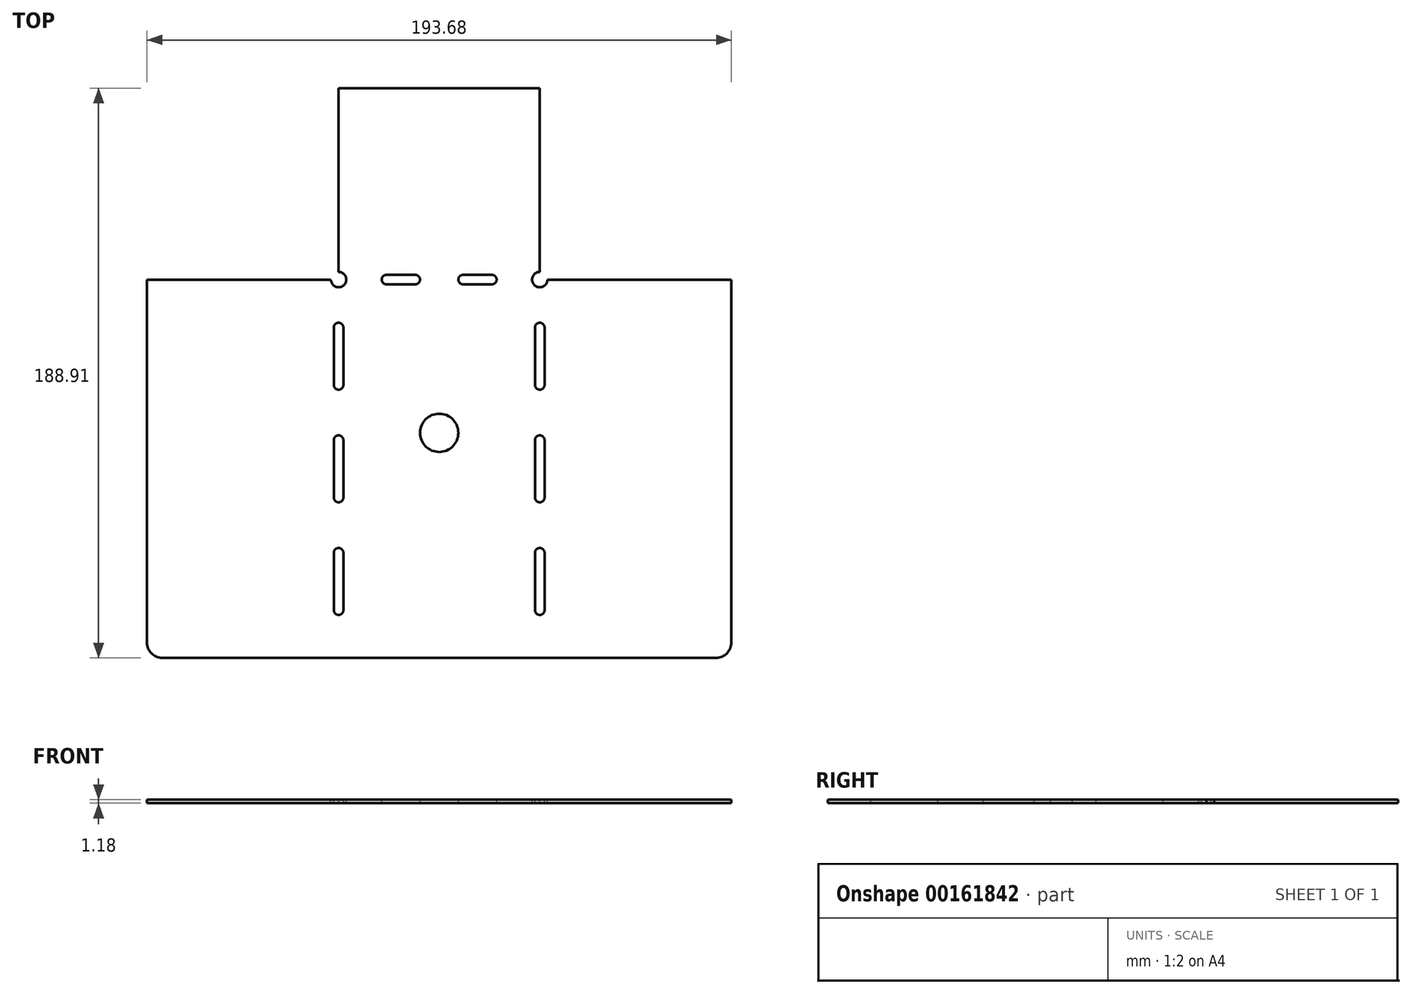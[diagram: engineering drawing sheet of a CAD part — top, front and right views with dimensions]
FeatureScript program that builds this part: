
annotation { "Feature Type Name" : "Feature", "Feature Type Description" : "" }
export const myFeature = defineFeature(function(context is Context, id is Id, definition is map)
    precondition{}
    {
        {
            var Q0;
            Q0=qCreatedBy(makeId("Top.planeOp"),FACE);
            var sketch = newSketch(context, id + "F0", { "sketchPlane" : qUnion([Q0])});
            skLineSegment(sketch, "E0", {"start": v(-33.34, 0) * mm, "end": v(33.34, 0) * mm});
            skLineSegment(sketch, "E1", {"start": v(33.34, 0) * mm, "end": v(33.34, 125.41) * mm});
            skLineSegment(sketch, "E2", {"start": v(33.34, 125.41) * mm, "end": v(-33.34, 125.41) * mm});
            skLineSegment(sketch, "E3", {"start": v(-33.34, 125.41) * mm, "end": v(-33.34, 0) * mm});
            skLineSegment(sketch, "E4", {"start": v(-33.34, 125.41) * mm, "end": v(-96.84, 125.41) * mm});
            skLineSegment(sketch, "E5", {"start": v(-96.84, 125.41) * mm, "end": v(-96.84, 0) * mm});
            skLineSegment(sketch, "E6", {"start": v(-96.84, 0) * mm, "end": v(-33.34, 0) * mm});
            skLineSegment(sketch, "E7", {"start": v(33.34, 125.41) * mm, "end": v(96.84, 125.41) * mm});
            skLineSegment(sketch, "E8", {"start": v(96.84, 125.41) * mm, "end": v(96.84, 0) * mm});
            skLineSegment(sketch, "E9", {"start": v(96.84, 0) * mm, "end": v(33.34, 0) * mm});
            skLineSegment(sketch, "E10", {"start": v(33.34, 125.41) * mm, "end": v(33.34, 188.91) * mm});
            skLineSegment(sketch, "E11", {"start": v(33.34, 188.91) * mm, "end": v(-33.34, 188.91) * mm});
            skLineSegment(sketch, "E12", {"start": v(-33.34, 188.91) * mm, "end": v(-33.34, 125.41) * mm});
            skSolve(sketch);
        }
        {
            var Q0;
            Q0 = qSketchRegion(id + "F0", true);
            extrude(context, id + "F1", {"entities" : qUnion([Q0]), "depth" : 1.18 * mm});
        }
        {
            var Q0;
            Q0=makeQuery(id+"F1.opExtrude","CAP_FACE",FACE,{"disambiguationData":[OSD([sQuery(id+"F0.wireOp",EDGE,"E0"),sQuery(id+"F0.wireOp",EDGE,"E4"),sQuery(id+"F0.wireOp",EDGE,"E5"),sQuery(id+"F0.wireOp",EDGE,"E6"),sQuery(id+"F0.wireOp",EDGE,"E7"),sQuery(id+"F0.wireOp",EDGE,"E8"),sQuery(id+"F0.wireOp",EDGE,"E9"),sQuery(id+"F0.wireOp",EDGE,"E10"),sQuery(id+"F0.wireOp",EDGE,"E11"),sQuery(id+"F0.wireOp",EDGE,"E12")])],"isStart":false});
            var sketch = newSketch(context, id + "F2", { "sketchPlane" : qUnion([Q0])});
            skLineSegment(sketch, "E13", {"start": v(-33.34, 109.54) * mm, "end": v(-33.34, 90.49) * mm});
            skLineSegment(sketch, "E14", {"start": v(0, 211.66) * mm, "end": v(0, -16) * mm, "construction": true});
            skLineSegment(sketch, "E15", {"start": v(-17.46, 125.41) * mm, "end": v(-7.94, 125.41) * mm});
            skPoint(sketch, "E16", {"position": v(-33.34, 109.54) * mm});
            skPoint(sketch, "E17", {"position": v(-33.34, 90.49) * mm});
            skPoint(sketch, "E18.orphan", {"position": v(-33.34, 0) * mm});
            skLineSegment(sketch, "E19.0.1.0", {"start": v(-33.34, 72.2) * mm, "end": v(-33.34, 53.15) * mm});
            skLineSegment(sketch, "E19.0.2.0", {"start": v(-33.34, 34.86) * mm, "end": v(-33.34, 15.81) * mm});
            skLineSegment(sketch, "E19.direction1", {"start": v(-33.34, 90.49) * mm, "end": v(-7.94, 90.49) * mm, "construction": true});
            skLineSegment(sketch, "E19.direction2", {"start": v(-33.34, 72.2) * mm, "end": v(-33.34, 53.15) * mm, "construction": true});
            skLineSegment(sketch, "E20.MirrorCS", {"start": v(33.34, 109.54) * mm, "end": v(33.34, 90.49) * mm});
            skLineSegment(sketch, "E21.MirrorCS", {"start": v(33.34, 72.2) * mm, "end": v(33.34, 53.15) * mm, "construction": true});
            skLineSegment(sketch, "E22.MirrorCS", {"start": v(33.34, 34.86) * mm, "end": v(33.34, 15.81) * mm});
            skArc(sketch, "E23.0.startCap", {"start": v(-34.93, 109.54) * mm, "mid": v(-33.34, 111.13) * mm, "end": v(-31.75, 109.54) * mm});
            skArc(sketch, "E23.0.endCap", {"start": v(-31.75, 90.49) * mm, "mid": v(-33.34, 88.9) * mm, "end": v(-34.93, 90.49) * mm});
            skLineSegment(sketch, "E23.0.left", {"start": v(-31.75, 109.54) * mm, "end": v(-31.75, 90.49) * mm});
            skLineSegment(sketch, "E23.0.right", {"start": v(-34.93, 109.54) * mm, "end": v(-34.93, 90.49) * mm});
            skArc(sketch, "E23.1.startCap", {"start": v(-34.93, 72.2) * mm, "mid": v(-33.34, 73.79) * mm, "end": v(-31.75, 72.2) * mm});
            skArc(sketch, "E23.1.endCap", {"start": v(-31.75, 53.15) * mm, "mid": v(-33.34, 51.56) * mm, "end": v(-34.93, 53.15) * mm});
            skLineSegment(sketch, "E23.1.left", {"start": v(-31.75, 72.2) * mm, "end": v(-31.75, 53.15) * mm});
            skLineSegment(sketch, "E23.1.right", {"start": v(-34.92, 72.2) * mm, "end": v(-34.92, 53.15) * mm});
            skArc(sketch, "E23.2.startCap", {"start": v(-34.93, 34.86) * mm, "mid": v(-33.34, 36.45) * mm, "end": v(-31.75, 34.86) * mm});
            skArc(sketch, "E23.2.endCap", {"start": v(-31.75, 15.81) * mm, "mid": v(-33.34, 14.22) * mm, "end": v(-34.93, 15.81) * mm});
            skLineSegment(sketch, "E23.2.left", {"start": v(-31.75, 34.86) * mm, "end": v(-31.75, 15.81) * mm});
            skLineSegment(sketch, "E23.2.right", {"start": v(-34.92, 34.86) * mm, "end": v(-34.92, 15.81) * mm});
            skArc(sketch, "E23.3.startCap", {"start": v(31.75, 34.86) * mm, "mid": v(33.34, 36.45) * mm, "end": v(34.93, 34.86) * mm});
            skArc(sketch, "E23.3.endCap", {"start": v(34.93, 15.81) * mm, "mid": v(33.34, 14.22) * mm, "end": v(31.75, 15.81) * mm});
            skLineSegment(sketch, "E23.3.left", {"start": v(34.93, 34.86) * mm, "end": v(34.93, 15.81) * mm});
            skLineSegment(sketch, "E23.3.right", {"start": v(31.75, 34.86) * mm, "end": v(31.75, 15.81) * mm});
            skArc(sketch, "E23.4.startCap", {"start": v(31.75, 72.2) * mm, "mid": v(33.34, 73.79) * mm, "end": v(34.93, 72.2) * mm});
            skArc(sketch, "E23.4.endCap", {"start": v(34.93, 53.15) * mm, "mid": v(33.34, 51.56) * mm, "end": v(31.75, 53.15) * mm});
            skLineSegment(sketch, "E23.4.left", {"start": v(34.93, 72.2) * mm, "end": v(34.93, 53.15) * mm});
            skLineSegment(sketch, "E23.4.right", {"start": v(31.75, 72.2) * mm, "end": v(31.75, 53.15) * mm});
            skArc(sketch, "E23.5.startCap", {"start": v(31.75, 109.54) * mm, "mid": v(33.34, 111.13) * mm, "end": v(34.93, 109.54) * mm});
            skArc(sketch, "E23.5.endCap", {"start": v(34.93, 90.49) * mm, "mid": v(33.34, 88.9) * mm, "end": v(31.75, 90.49) * mm});
            skLineSegment(sketch, "E23.5.left", {"start": v(34.93, 109.54) * mm, "end": v(34.93, 90.49) * mm});
            skLineSegment(sketch, "E23.5.right", {"start": v(31.75, 109.54) * mm, "end": v(31.75, 90.49) * mm});
            skPoint(sketch, "E24", {"position": v(-17.46, 125.41) * mm});
            skPoint(sketch, "E25", {"position": v(-7.94, 125.41) * mm});
            skPoint(sketch, "E26", {"position": v(7.94, 125.41) * mm});
            skPoint(sketch, "E27", {"position": v(17.46, 125.41) * mm});
            skPoint(sketch, "E28.orphan", {"position": v(-33.34, 125.41) * mm});
            skPoint(sketch, "E29.orphan", {"position": v(33.34, 125.41) * mm});
            skLineSegment(sketch, "E30.trimOffspring", {"start": v(7.94, 125.41) * mm, "end": v(17.46, 125.41) * mm});
            skArc(sketch, "E31.0.startCap", {"start": v(-17.46, 123.83) * mm, "mid": v(-19.05, 125.41) * mm, "end": v(-17.46, 127) * mm});
            skArc(sketch, "E31.0.endCap", {"start": v(-7.94, 127) * mm, "mid": v(-6.35, 125.41) * mm, "end": v(-7.94, 123.83) * mm});
            skLineSegment(sketch, "E31.0.left", {"start": v(-17.46, 127) * mm, "end": v(-7.94, 127) * mm});
            skLineSegment(sketch, "E31.0.right", {"start": v(-17.46, 123.83) * mm, "end": v(-7.94, 123.83) * mm});
            skArc(sketch, "E31.1.startCap", {"start": v(7.94, 123.83) * mm, "mid": v(6.35, 125.41) * mm, "end": v(7.94, 127) * mm});
            skArc(sketch, "E31.1.endCap", {"start": v(17.46, 127) * mm, "mid": v(19.05, 125.41) * mm, "end": v(17.46, 123.83) * mm});
            skLineSegment(sketch, "E31.1.left", {"start": v(7.94, 127) * mm, "end": v(17.46, 127) * mm});
            skLineSegment(sketch, "E31.1.right", {"start": v(7.94, 123.83) * mm, "end": v(17.46, 123.83) * mm});
            skCircle(sketch, "E32", {"center": v(-33.34, 125.41) * mm, "radius": 2.54 * mm});
            skCircle(sketch, "E33", {"center": v(33.34, 125.41) * mm, "radius": 2.54 * mm});
            skCircle(sketch, "E34", {"center": v(0, 74.61) * mm, "radius": 6.35 * mm});
            skSolve(sketch);
        }
        {
            var Q0;
            Q0 = qSketchRegion(id + "F2", true);
            extrude(context, id + "F3", {"entities" : qUnion([Q0]), "operationType" : NewBodyOperationType.REMOVE, "endBound" : BoundingType.UP_TO_NEXT, "oppositeDirection" : true, "depth" : 25.4 * mm});
        }
        {
            var Q0;
            Q0=makeQuery(id+"F1.opExtrude","SWEPT_EDGE",EDGE,{"disambiguationData":[OSD([sQuery(id+"F0.wireOp",EDGE,"E5"),sQuery(id+"F0.wireOp",EDGE,"E6")])]});
            var Q1;
            Q1=makeQuery(id+"F1.opExtrude","SWEPT_EDGE",EDGE,{"disambiguationData":[OSD([sQuery(id+"F0.wireOp",EDGE,"E8"),sQuery(id+"F0.wireOp",EDGE,"E9")])]});
            fillet(context, id + "F4", {"entities" : qUnion([Q0, Q1]), "radius" : 5.08 * mm, "tangentPropagation" : true, "allowEdgeOverflow" : false});
        }
    });
